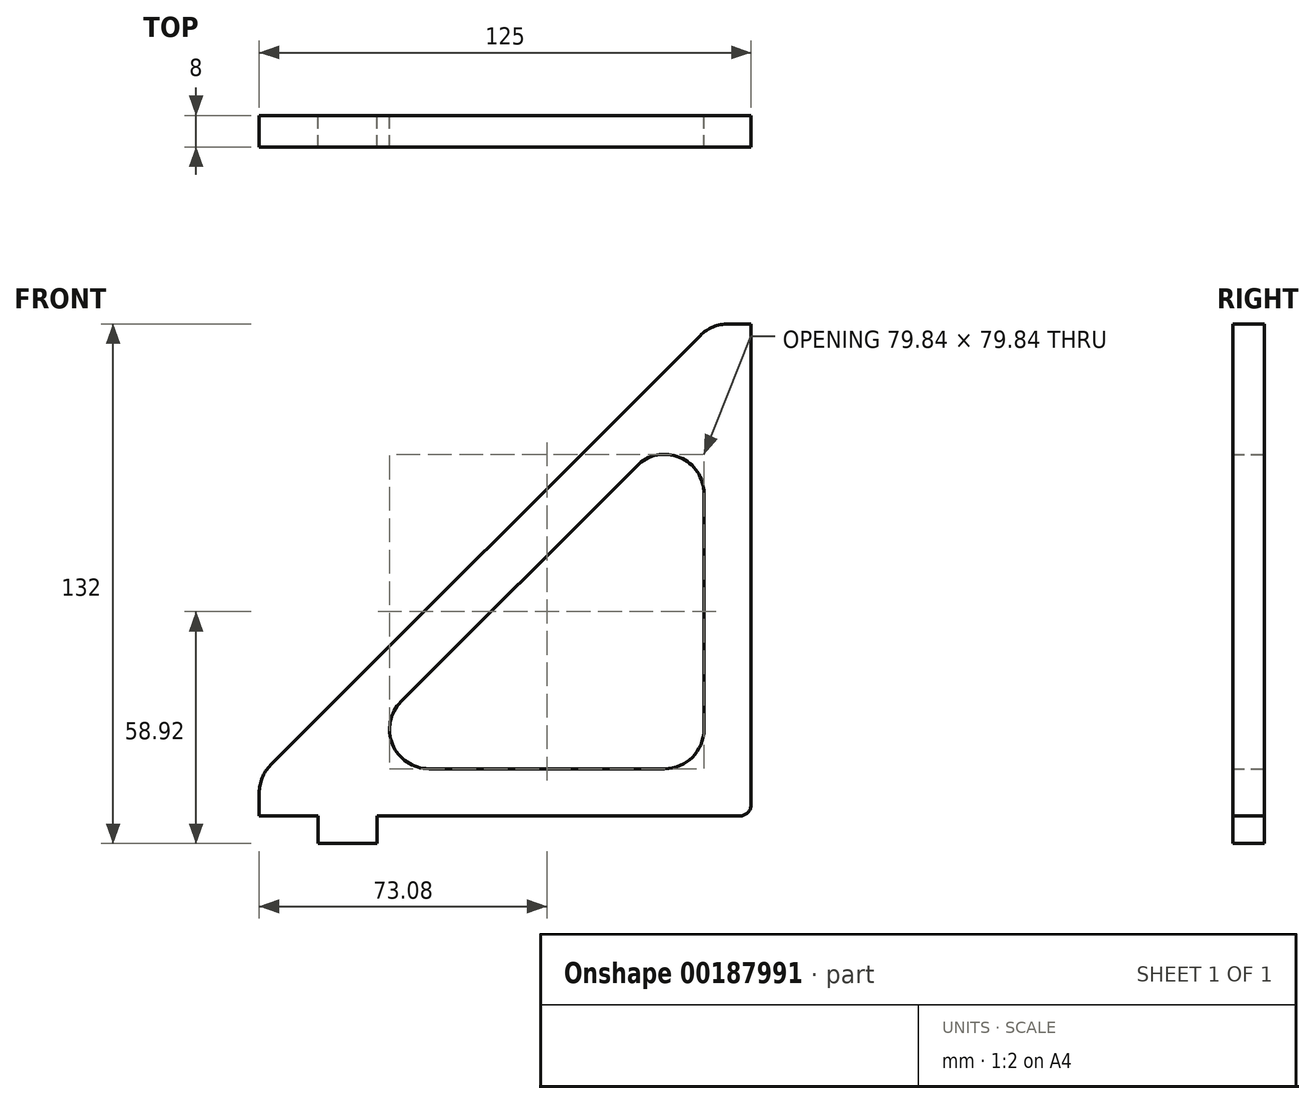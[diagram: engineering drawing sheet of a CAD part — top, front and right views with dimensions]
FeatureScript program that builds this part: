
annotation { "Feature Type Name" : "Feature", "Feature Type Description" : "" }
export const myFeature = defineFeature(function(context is Context, id is Id, definition is map)
    precondition{}
    {
        {
            var Q0;
            Q0=qCreatedBy(makeId("Front.planeOp"),FACE);
            var sketch = newSketch(context, id + "F0", { "sketchPlane" : qUnion([Q0])});
            skLineSegment(sketch, "E0", {"start": v(0, 3) * mm, "end": v(0, 125) * mm});
            skLineSegment(sketch, "E1", {"start": v(0, 125) * mm, "end": v(-5.86, 125) * mm});
            skLineSegment(sketch, "E2", {"start": v(-12.93, 122.07) * mm, "end": v(-122.07, 12.93) * mm});
            skLineSegment(sketch, "E3", {"start": v(-125, 5.86) * mm, "end": v(-125, 0) * mm});
            skLineSegment(sketch, "E4", {"start": v(-125, 0) * mm, "end": v(-110, 0) * mm});
            skLineSegment(sketch, "E5", {"start": v(-95, 0) * mm, "end": v(-95, -7) * mm});
            skLineSegment(sketch, "E6", {"start": v(-95, -7) * mm, "end": v(-110, -7) * mm});
            skLineSegment(sketch, "E7", {"start": v(-110, -7) * mm, "end": v(-110, 0) * mm});
            skPoint(sketch, "E8.visualSharp", {"position": v(-125, 10) * mm});
            skArc(sketch, "E8.filletArc", {"start": v(-122.07, 12.93) * mm, "mid": v(-124.24, 9.68) * mm, "end": v(-125, 5.86) * mm});
            skPoint(sketch, "E9.visualSharp", {"position": v(-10, 125) * mm});
            skArc(sketch, "E9.filletArc", {"start": v(-5.86, 125) * mm, "mid": v(-9.68, 124.24) * mm, "end": v(-12.93, 122.07) * mm});
            skLineSegment(sketch, "E10", {"start": v(-12, 81.89) * mm, "end": v(-12, 22) * mm});
            skLineSegment(sketch, "E11", {"start": v(-22, 12) * mm, "end": v(-81.89, 12) * mm});
            skLineSegment(sketch, "E12", {"start": v(-88.96, 29.07) * mm, "end": v(-29.07, 88.96) * mm});
            skPoint(sketch, "E13.visualSharp", {"position": v(-106.03, 12) * mm});
            skArc(sketch, "E13.filletArc", {"start": v(-88.96, 29.07) * mm, "mid": v(-91.13, 18.17) * mm, "end": v(-81.89, 12) * mm});
            skPoint(sketch, "E14.visualSharp", {"position": v(-12, 12) * mm});
            skArc(sketch, "E14.filletArc", {"start": v(-22, 12) * mm, "mid": v(-14.93, 14.93) * mm, "end": v(-12, 22) * mm});
            skPoint(sketch, "E15.visualSharp", {"position": v(-12, 106.03) * mm});
            skArc(sketch, "E15.filletArc", {"start": v(-12, 81.89) * mm, "mid": v(-18.17, 91.13) * mm, "end": v(-29.07, 88.96) * mm});
            skLineSegment(sketch, "E16.trimOffspring", {"start": v(-95, 0) * mm, "end": v(-3, 0) * mm});
            skPoint(sketch, "E17.visualSharp", {"position": v(0, 0) * mm});
            skArc(sketch, "E17.filletArc", {"start": v(-3, 0) * mm, "mid": v(-0.88, 0.88) * mm, "end": v(0, 3) * mm});
            skSolve(sketch);
        }
        {
            var Q0;
            Q0=makeQuery(id+"F0.imprint","IMPRINT",FACE,{"disambiguationData":[TD([[makeQuery(id+"F0.imprint","IMPRINT",EDGE,{"derivedFrom":sQuery(id+"F0.wireOp",EDGE,"E0")}),1.0]])]});
            extrude(context, id + "F1", {"entities" : qUnion([Q0]), "depth" : 8 * mm});
        }
    });
